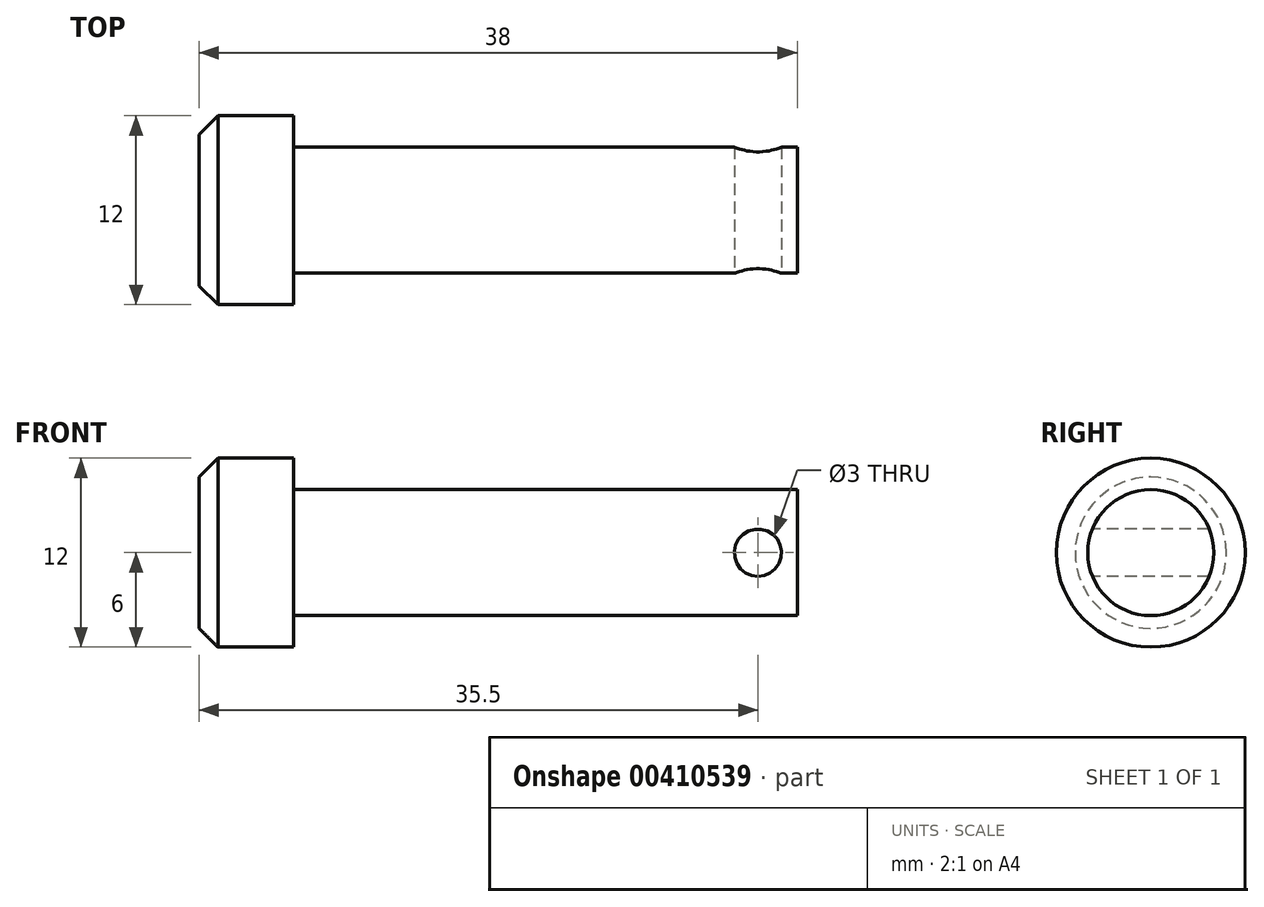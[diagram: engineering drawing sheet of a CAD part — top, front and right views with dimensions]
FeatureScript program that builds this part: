
annotation { "Feature Type Name" : "Feature", "Feature Type Description" : "" }
export const myFeature = defineFeature(function(context is Context, id is Id, definition is map)
    precondition{}
    {
        {
            var Q0;
            Q0=qCreatedBy(makeId("Right.planeOp"),FACE);
            var sketch = newSketch(context, id + "F0", { "sketchPlane" : qUnion([Q0])});
            skCircle(sketch, "E0", {"center": v(0, 0) * mm, "radius": 6 * mm});
            skCircle(sketch, "E1", {"center": v(0, 0) * mm, "radius": 4 * mm});
            skSolve(sketch);
        }
        {
            var Q0;
            Q0=makeQuery(id+"F0.imprint","IMPRINT",FACE,{"disambiguationData":[TD([[makeQuery(id+"F0.imprint","IMPRINT",EDGE,{"derivedFrom":sQuery(id+"F0.wireOp",EDGE,"E1")}),1.0]])]});
            extrude(context, id + "F1", {"entities" : qUnion([Q0]), "depth" : 38 * mm});
        }
        {
            var Q0;
            Q0=makeQuery(id+"F0.imprint","IMPRINT",FACE,{"disambiguationData":[TD([[makeQuery(id+"F0.imprint","IMPRINT",EDGE,{"derivedFrom":sQuery(id+"F0.wireOp",EDGE,"E0")}),1.0]])]});
            extrude(context, id + "F2", {"entities" : qUnion([Q0]), "operationType" : NewBodyOperationType.ADD, "depth" : 6 * mm});
        }
        {
            var Q0;
            Q0=makeQuery(id+"F2.opExtrude","CAP_EDGE",EDGE,{"disambiguationData":[OSD([sQuery(id+"F0.wireOp",EDGE,"E0")])],"isStart":true});
            chamfer(context, id + "F3", {"entities" : qUnion([Q0]), "width" : 1.2 * mm, "tangentPropagation" : true});
        }
        {
            var Q0;
            Q0=qCreatedBy(makeId("Front.planeOp"),FACE);
            var sketch = newSketch(context, id + "F4", { "sketchPlane" : qUnion([Q0])});
            skCircle(sketch, "E2", {"center": v(35.5, 0) * mm, "radius": 1.5 * mm});
            skSolve(sketch);
        }
        {
            var Q0;
            Q0 = qSketchRegion(id + "F4", true);
            extrude(context, id + "F5", {"entities" : qUnion([Q0]), "operationType" : NewBodyOperationType.REMOVE, "oppositeDirection" : true, "depth" : 8 * mm, "symmetric" : true});
        }
    });
